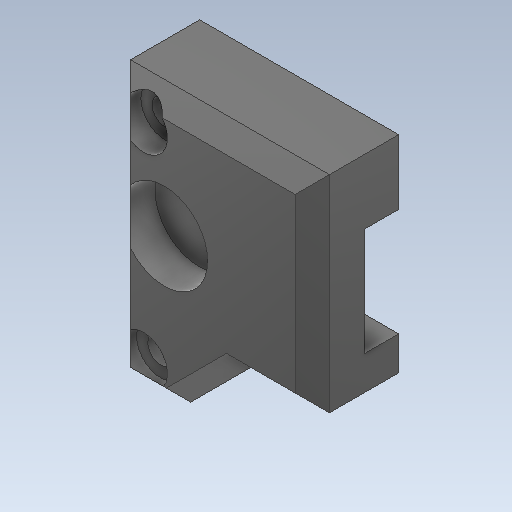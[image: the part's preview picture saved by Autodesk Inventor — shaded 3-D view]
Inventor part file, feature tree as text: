
AUTODESK INVENTOR PART (.ipt)
format: ipt  version: 2020 (Build 240168000, 168)  size: 250,368 bytes
history: native  units: in
note: dims shown in document units (in); Inventor stores cm internally (conversion verified against a paired STEP export)
features: sketch x30, other x3, plane x1
ambient origin geometry x8: Origin, YZ Plane, XZ Plane, XY Plane, X Axis, Y Axis, Z Axis, Center Point
bodies: Solid1 (feature_tree)
feature tree (34):
  other  "FermurSupportSup.ipt"
  other  "Solid1::FermurSupportSup.ipt"
  other  "TaggingFeature1"
  sketch  "Sketch1"  dims[d0=0.3937in]
  sketch  "Sketch2"
  sketch  "Sketch3"
  sketch  "Sketch4"
  sketch  "Sketch5"
  sketch  "Sketch6"
  sketch  "Sketch8"
  sketch  "Sketch10"
  sketch  "Sketch11"
  sketch  "Sketch12"
  sketch  "Sketch13"
  sketch  "Sketch14"
  sketch  "Sketch15"
  sketch  "Sketch17"
  sketch  "Sketch19"
  sketch  "Sketch21"
  sketch  "Sketch22"
  sketch  "Sketch23"
  sketch  "Sketch24"
  sketch  "Sketch25"
  sketch  "Sketch26"
  sketch  "Sketch27"
  sketch  "Sketch29"
  sketch  "Sketch32"
  sketch  "Sketch33"
  sketch  "Sketch36"
  sketch  "Sketch37"
  sketch  "Sketch38"
  sketch  "Sketch39"
  sketch  "Sketch40"
  plane  "Work Plane1"
